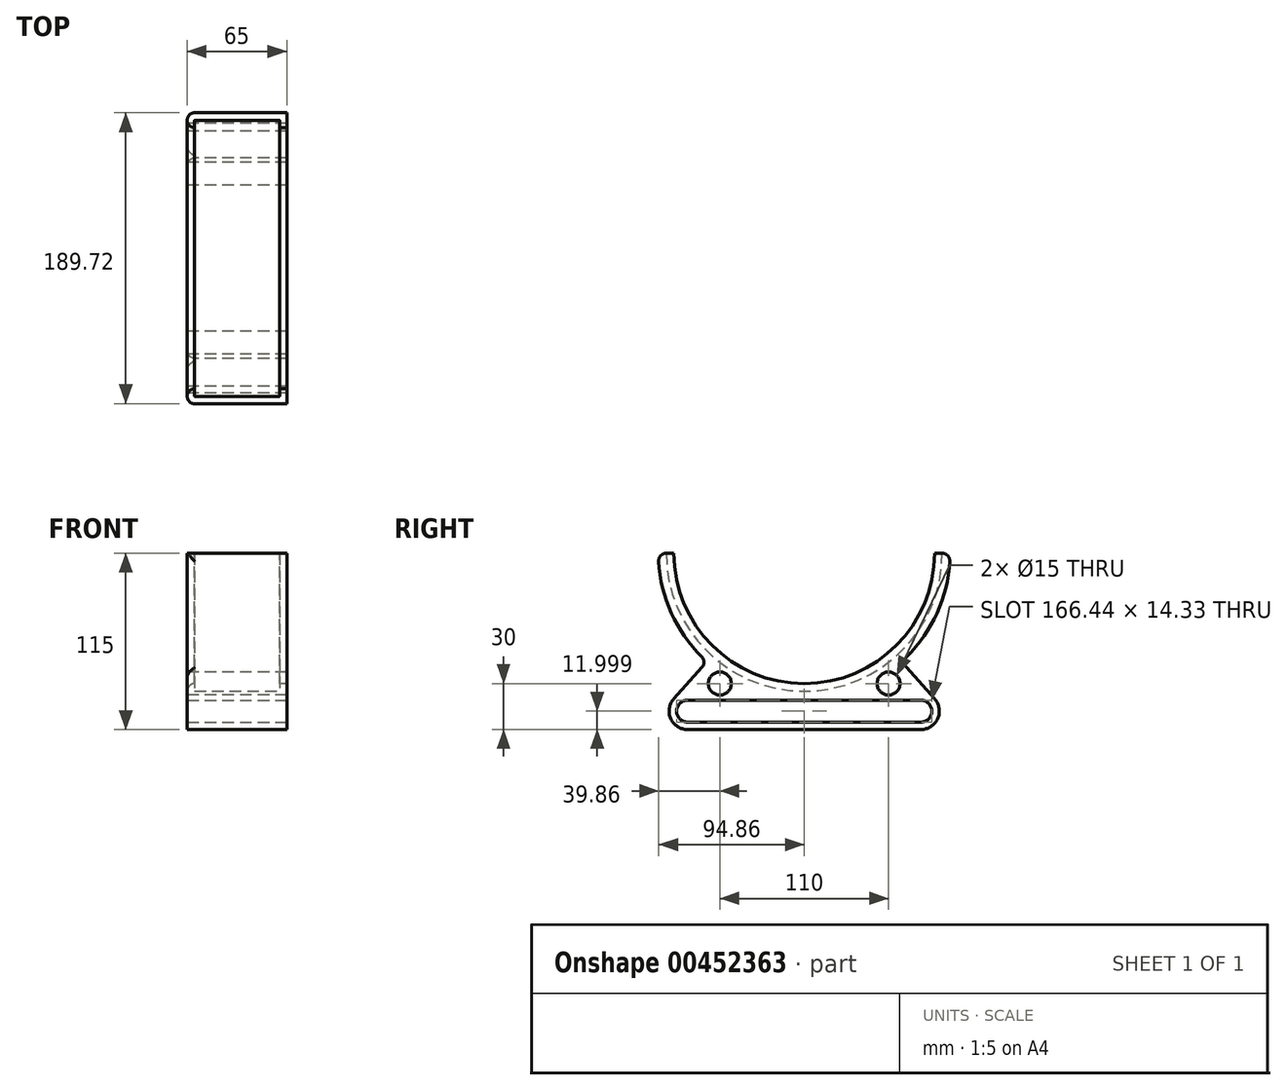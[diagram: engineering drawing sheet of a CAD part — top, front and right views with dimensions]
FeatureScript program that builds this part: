
annotation { "Feature Type Name" : "Feature", "Feature Type Description" : "" }
export const myFeature = defineFeature(function(context is Context, id is Id, definition is map)
    precondition{}
    {
        {
            var Q0;
            Q0=qCreatedBy(makeId("Right.planeOp"),FACE);
            var sketch = newSketch(context, id + "F0", { "sketchPlane" : qUnion([Q0])});
            skArc(sketch, "E0", {"start": v(-85, 95) * mm, "mid": v(0, 10) * mm, "end": v(85, 95) * mm});
            skArc(sketch, "E1", {"start": v(-95, 95) * mm, "mid": v(-86.73, 56.22) * mm, "end": v(-63.35, 24.2) * mm});
            skLineSegment(sketch, "E2", {"start": v(-95, 95) * mm, "end": v(-85, 95) * mm});
            skLineSegment(sketch, "E3", {"start": v(85, 95) * mm, "end": v(95, 95) * mm});
            skLineSegment(sketch, "E4", {"start": v(0, 0) * mm, "end": v(-85, 0) * mm, "construction": true});
            skLineSegment(sketch, "E5", {"start": v(-85, 0) * mm, "end": v(-63.35, 24.2) * mm});
            skLineSegment(sketch, "E6.MirrorCS", {"start": v(0, 0) * mm, "end": v(85, 0) * mm, "construction": true});
            skLineSegment(sketch, "E7.MirrorCS", {"start": v(85, 0) * mm, "end": v(63.35, 24.2) * mm});
            skArc(sketch, "E8.trimOffspring", {"start": v(63.35, 24.2) * mm, "mid": v(86.73, 56.22) * mm, "end": v(95, 95) * mm});
            skLineSegment(sketch, "E9", {"start": v(-63.35, 24.2) * mm, "end": v(-89.05, 47.2) * mm, "construction": true});
            skCircle(sketch, "E10", {"center": v(-55, 10) * mm, "radius": 7.5 * mm});
            skCircle(sketch, "E11.MirrorC", {"center": v(55, 10) * mm, "radius": 7.5 * mm});
            skArc(sketch, "E12", {"start": v(-85, 0) * mm, "mid": v(-87.01, -12.9) * mm, "end": v(-76.06, -20) * mm});
            skArc(sketch, "E13", {"start": v(76.06, -20) * mm, "mid": v(87.01, -12.9) * mm, "end": v(85, 0) * mm});
            skLineSegment(sketch, "E14", {"start": v(-76.06, -20) * mm, "end": v(76.06, -20) * mm});
            skSolve(sketch);
        }
        {
            var Q0;
            Q0 = qSketchRegion(id + "F0", true);
            extrude(context, id + "F1", {"entities" : qUnion([Q0]), "endBound" : BoundingType.SYMMETRIC, "depth" : 65 * mm});
        }
        {
            var Q0;
            Q0=qCreatedBy(makeId("Right.planeOp"),FACE);
            var sketch = newSketch(context, id + "F2", { "sketchPlane" : qUnion([Q0])});
            skArc(sketch, "E15", {"start": v(-90, 95) * mm, "mid": v(0, 5) * mm, "end": v(90, 95) * mm});
            skArc(sketch, "E16", {"start": v(-85, 95) * mm, "mid": v(0, 10) * mm, "end": v(85, 95) * mm});
            skLineSegment(sketch, "E17", {"start": v(-90, 95) * mm, "end": v(-85, 95) * mm});
            skLineSegment(sketch, "E18", {"start": v(85, 95) * mm, "end": v(90, 95) * mm});
            skSolve(sketch);
        }
        {
            var Q0;
            Q0 = qSketchRegion(id + "F2", true);
            extrude(context, id + "F3", {"entities" : qUnion([Q0]), "operationType" : NewBodyOperationType.REMOVE, "endBound" : BoundingType.SYMMETRIC, "oppositeDirection" : true, "depth" : 55.5 * mm});
        }
        {
            var Q0;
            Q0=makeQuery(id+"F1.opExtrude","SWEPT_EDGE",EDGE,{"disambiguationData":[OSD([sQuery(id+"F0.wireOp",EDGE,"E1"),sQuery(id+"F0.wireOp",EDGE,"E2")])]});
            var Q1;
            Q1=makeQuery(id+"F1.opExtrude","SWEPT_EDGE",EDGE,{"disambiguationData":[OSD([sQuery(id+"F0.wireOp",EDGE,"E3"),sQuery(id+"F0.wireOp",EDGE,"E8.trimOffspring")])]});
            var Q2;
            Q2=makeQuery(id+"F1.opExtrude","SWEPT_EDGE",EDGE,{"disambiguationData":[OSD([sQuery(id+"F0.wireOp",EDGE,"E1"),sQuery(id+"F0.wireOp",EDGE,"E5")])]});
            var Q3;
            Q3=makeQuery(id+"F1.opExtrude","SWEPT_EDGE",EDGE,{"disambiguationData":[OSD([sQuery(id+"F0.wireOp",EDGE,"E7.MirrorCS"),sQuery(id+"F0.wireOp",EDGE,"E8.trimOffspring")])]});
            var Q4;
            Q4=makeQuery(id+"F1.opExtrude","CAP_EDGE",EDGE,{"disambiguationData":[OSD([sQuery(id+"F0.wireOp",EDGE,"E1")])],"isStart":true});
            var Q5;
            Q5=makeQuery(id+"F1.opExtrude","CAP_EDGE",EDGE,{"disambiguationData":[OSD([sQuery(id+"F0.wireOp",EDGE,"E8.trimOffspring")])],"isStart":true});
            fillet(context, id + "F4", {"entities" : qUnion([Q0, Q1, Q2, Q3, Q4, Q5]), "radius" : 5 * mm, "tangentPropagation" : true, "allowEdgeOverflow" : false});
        }
        {
            var Q0;
            Q0=makeQuery(id+"F1.opExtrude","CAP_EDGE",EDGE,{"disambiguationData":[OSD([sQuery(id+"F0.wireOp",EDGE,"E0")])],"isStart":true});
            fillet(context, id + "F5", {"entities" : qUnion([Q0]), "radius" : 5 * mm, "tangentPropagation" : true, "allowEdgeOverflow" : false});
        }
        {
            var Q0;
            Q0=makeQuery(id+"F1.opExtrude","CAP_FACE",FACE,{"disambiguationData":[OSD([sQuery(id+"F0.wireOp",EDGE,"E0"),sQuery(id+"F0.wireOp",EDGE,"E1"),sQuery(id+"F0.wireOp",EDGE,"E2"),sQuery(id+"F0.wireOp",EDGE,"E3"),sQuery(id+"F0.wireOp",EDGE,"E5"),sQuery(id+"F0.wireOp",EDGE,"E7.MirrorCS"),sQuery(id+"F0.wireOp",EDGE,"E8.trimOffspring"),sQuery(id+"F0.wireOp",EDGE,"E10"),sQuery(id+"F0.wireOp",EDGE,"E11.MirrorC"),sQuery(id+"F0.wireOp",EDGE,"E12"),sQuery(id+"F0.wireOp",EDGE,"E13"),sQuery(id+"F0.wireOp",EDGE,"E14")])],"isStart":false});
            var sketch = newSketch(context, id + "F6", { "sketchPlane" : qUnion([Q0])});
            skArc(sketch, "E19", {"start": v(-76.06, -0.84) * mm, "mid": v(-83.22, -8) * mm, "end": v(-76.06, -15.16) * mm});
            skLineSegment(sketch, "E20", {"start": v(-76.06, -0.84) * mm, "end": v(76.06, -0.84) * mm});
            skArc(sketch, "E21", {"start": v(76.06, -15.16) * mm, "mid": v(83.22, -8) * mm, "end": v(76.06, -0.84) * mm});
            skLineSegment(sketch, "E22", {"start": v(76.06, -15.16) * mm, "end": v(-76.06, -15.16) * mm});
            skSolve(sketch);
        }
        {
            var Q0;
            Q0 = qSketchRegion(id + "F6", true);
            extrude(context, id + "F7", {"entities" : qUnion([Q0]), "operationType" : NewBodyOperationType.REMOVE, "endBound" : BoundingType.THROUGH_ALL, "oppositeDirection" : true, "depth" : 25 * mm});
        }
    });
